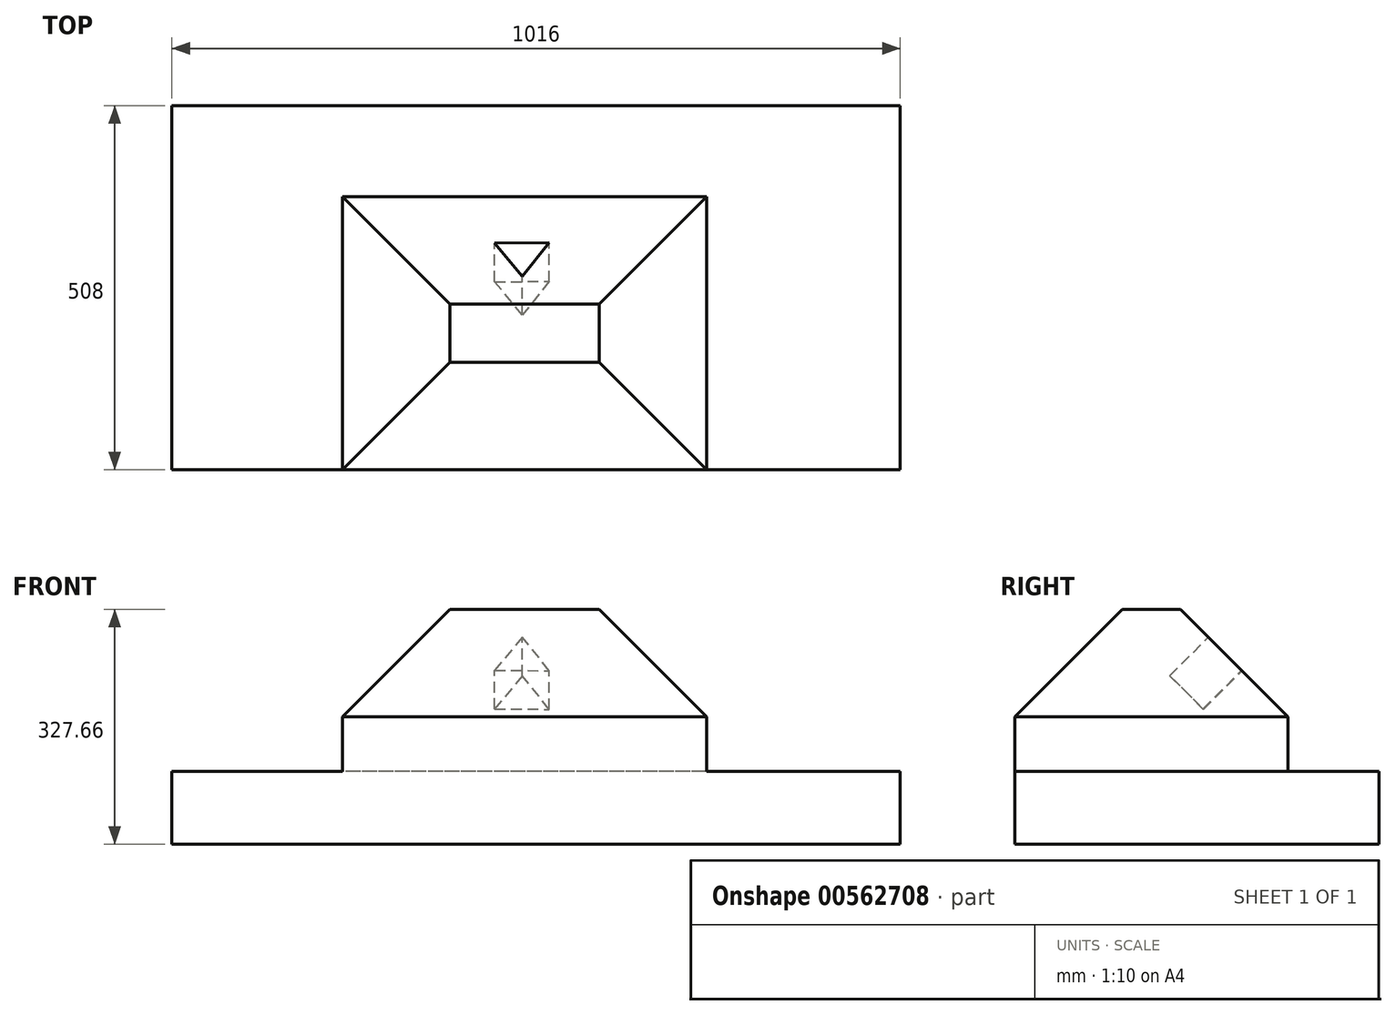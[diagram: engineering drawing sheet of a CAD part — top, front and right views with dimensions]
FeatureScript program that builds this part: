
annotation { "Feature Type Name" : "Feature", "Feature Type Description" : "" }
export const myFeature = defineFeature(function(context is Context, id is Id, definition is map)
    precondition{}
    {
        {
            var Q0;
            Q0=qCreatedBy(makeId("Top.planeOp"),FACE);
            var sketch = newSketch(context, id + "F0", { "sketchPlane" : qUnion([Q0])});
            skLineSegment(sketch, "E0.bottom", {"start": v(508, 254) * mm, "end": v(-508, 254) * mm});
            skLineSegment(sketch, "E0.top", {"start": v(508, -254) * mm, "end": v(-508, -254) * mm});
            skLineSegment(sketch, "E0.left", {"start": v(508, 254) * mm, "end": v(508, -254) * mm});
            skLineSegment(sketch, "E0.right", {"start": v(-508, 254) * mm, "end": v(-508, -254) * mm});
            skPoint(sketch, "E0.middle", {"position": v(0, 0) * mm});
            skSolve(sketch);
        }
        {
            var Q0;
            Q0=qSketchRegion(id+"F0",true);
            extrude(context, id + "F1", {"entities" : qUnion([Q0]), "depth" : 101.6 * mm, "offsetDistance" : 25.4 * mm});
        }
        {
            var Q0;
            Q0=makeQuery(id+"F1.opExtrude","CAP_FACE",FACE,{"disambiguationData":[OSD([sQuery(id+"F0.wireOp",EDGE,"E0.bottom"),sQuery(id+"F0.wireOp",EDGE,"E0.top"),sQuery(id+"F0.wireOp",EDGE,"E0.left"),sQuery(id+"F0.wireOp",EDGE,"E0.right")])],"isStart":true});
            var sketch = newSketch(context, id + "F2", { "sketchPlane" : qUnion([Q0])});
            skCircle(sketch, "E1", {"center": v(-404.68, 181.33) * mm, "radius": 53.59 * mm});
            skPoint(sketch, "E1.first.point", {"position": v(-448.8, 211.74) * mm});
            skPoint(sketch, "E1.second.point", {"position": v(-391.29, 129.44) * mm});
            skPoint(sketch, "E1.third.point", {"position": v(-355.59, 202.82) * mm});
            skCircle(sketch, "E2.MirrorC", {"center": v(404.68, 181.33) * mm, "radius": 53.59 * mm});
            skCircle(sketch, "E3.MirrorC", {"center": v(-404.68, -181.33) * mm, "radius": 53.59 * mm});
            skCircle(sketch, "E4.MirrorC", {"center": v(404.68, -181.33) * mm, "radius": 53.59 * mm});
            skSolve(sketch);
        }
        {
            var Q0;
            Q0=sQuery(id+"F2.wireOp",EDGE,"E1");
            var Q1;
            Q1=sQuery(id+"F2.wireOp",EDGE,"E3.MirrorC");
            var Q2;
            Q2=sQuery(id+"F2.wireOp",EDGE,"E2.MirrorC");
            var Q3;
            Q3=sQuery(id+"F2.wireOp",EDGE,"E4.MirrorC");
            extrude(context, id + "F3", {"bodyType" : ToolBodyType.SURFACE, "surfaceEntities" : qUnion([Q0, Q1, Q2, Q3]), "depth" : 762 * mm, "offsetDistance" : 25.4 * mm});
        }
        {
            var Q0;
            Q0=makeQuery(id+"F1.opExtrude","CAP_FACE",FACE,{"disambiguationData":[OSD([sQuery(id+"F0.wireOp",EDGE,"E0.bottom"),sQuery(id+"F0.wireOp",EDGE,"E0.top"),sQuery(id+"F0.wireOp",EDGE,"E0.left"),sQuery(id+"F0.wireOp",EDGE,"E0.right")])],"isStart":false});
            var sketch = newSketch(context, id + "F4", { "sketchPlane" : qUnion([Q0])});
            skLineSegment(sketch, "E5", {"start": v(0, -254) * mm, "end": v(0, 254) * mm});
            skLineSegment(sketch, "E6", {"start": v(237.95, -254) * mm, "end": v(237.95, 127) * mm});
            skLineSegment(sketch, "E7", {"start": v(237.95, 127) * mm, "end": v(-270.05, 127) * mm});
            skLineSegment(sketch, "E8", {"start": v(-270.05, 127) * mm, "end": v(-270.05, -254) * mm});
            skSolve(sketch);
        }
        {
            var Q0;
            {var subQ5=sQuery(id+"F4.wireOp",EDGE,"E6");Q0=makeQuery(id+"F4.imprint","IMPRINT",FACE,{"disambiguationData":[TD([[makeQuery(id+"F4.imprint","IMPRINT",EDGE,{"derivedFrom":subQ5}),1.0]])]});}
            var Q1;
            {var subQ5=sQuery(id+"F4.wireOp",EDGE,"E8");Q1=makeQuery(id+"F4.imprint","IMPRINT",FACE,{"disambiguationData":[TD([[makeQuery(id+"F4.imprint","IMPRINT",EDGE,{"derivedFrom":subQ5}),1.0]])]});}
            extrude(context, id + "F5", {"entities" : qUnion([Q0, Q1]), "operationType" : NewBodyOperationType.ADD, "depth" : 76.2 * mm, "offsetDistance" : 25.4 * mm});
        }
        {
            var Q0;
            Q0=makeQuery(id+"F5.opExtrude","CAP_FACE",FACE,{"disambiguationData":[OSD([sQuery(id+"F0.wireOp",EDGE,"E0.top"),sQuery(id+"F4.wireOp",EDGE,"E6"),sQuery(id+"F4.wireOp",EDGE,"E7"),sQuery(id+"F4.wireOp",EDGE,"E8")])],"isStart":false});
            extrude(context, id + "F6", {"entities" : qUnion([Q0]), "operationType" : NewBodyOperationType.ADD, "endBound" : BoundingType.SYMMETRIC, "depth" : 299.72 * mm, "offsetDistance" : 25.4 * mm, "hasDraft" : true, "draftAngle" : 45 * degree, "draftPullDirection" : true});
        }
        {
            var Q0;
            Q0=makeQuery(id+"F6.*.split.splitOp","SPLIT",FACE,{"derivedFrom":makeQuery(id+"F6.opExtrude","SWEPT_FACE",FACE,{"disambiguationData":[OSD([sQuery(id+"F4.wireOp",EDGE,"E7")])]})});
            var sketch = newSketch(context, id + "F7", { "sketchPlane" : qUnion([Q0])});
            skLineSegment(sketch, "E9.0", {"start": v(57.98, 127.63) * mm, "end": v(-18.22, 126.88) * mm});
            skLineSegment(sketch, "E9.1", {"start": v(-18.22, 126.88) * mm, "end": v(19.23, 193.24) * mm});
            skLineSegment(sketch, "E9.2", {"start": v(19.23, 193.24) * mm, "end": v(57.98, 127.63) * mm});
            skSolve(sketch);
        }
        {
            var Q0;
            Q0=makeQuery(id+"F7.imprint","IMPRINT",FACE,{"disambiguationData":[TD([[makeQuery(id+"F7.imprint","IMPRINT",EDGE,{"derivedFrom":sQuery(id+"F7.wireOp",EDGE,"E9.0")}),-1.0]])]});
            extrude(context, id + "F8", {"entities" : qUnion([Q0]), "operationType" : NewBodyOperationType.REMOVE, "oppositeDirection" : true, "depth" : 76.2 * mm, "offsetDistance" : 25.4 * mm});
        }
    });
